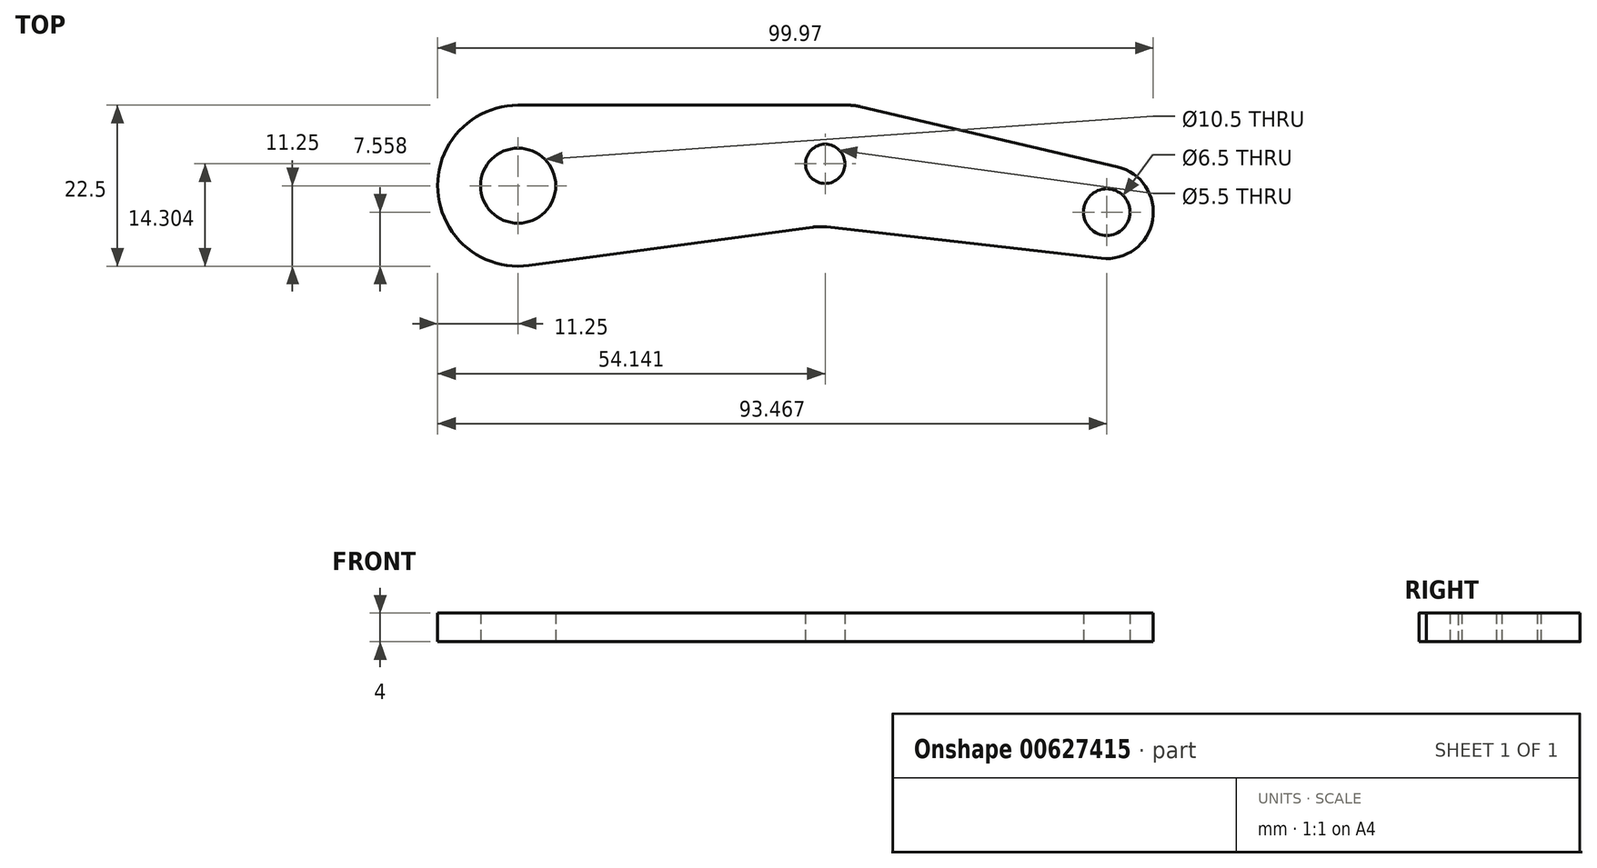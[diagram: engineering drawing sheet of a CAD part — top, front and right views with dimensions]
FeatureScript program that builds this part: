
annotation { "Feature Type Name" : "Feature", "Feature Type Description" : "" }
export const myFeature = defineFeature(function(context is Context, id is Id, definition is map)
    precondition{}
    {
        {
            var Q0;
            Q0=qCreatedBy(makeId("Top.planeOp"),FACE);
            var sketch = newSketch(context, id + "F0", { "sketchPlane" : qUnion([Q0])});
            skCircle(sketch, "E0", {"center": v(0, 0) * mm, "radius": 5.25 * mm});
            skArc(sketch, "E1", {"start": v(0, 11.25) * mm, "mid": v(-11.22, -0.76) * mm, "end": v(1.5, -11.15) * mm});
            skLineSegment(sketch, "E2", {"start": v(0, 11.25) * mm, "end": v(46.98, 11.25) * mm});
            skLineSegment(sketch, "E3", {"start": v(46.98, 11.25) * mm, "end": v(83.7, 2.64) * mm});
            skArc(sketch, "E4", {"start": v(81.48, -10.15) * mm, "mid": v(88.62, -4.8) * mm, "end": v(83.7, 2.64) * mm});
            skLineSegment(sketch, "E5", {"start": v(1.5, -11.15) * mm, "end": v(42.09, -5.66) * mm});
            skLineSegment(sketch, "E6", {"start": v(42.09, -5.66) * mm, "end": v(81.48, -10.15) * mm});
            skCircle(sketch, "E7", {"center": v(82.22, -3.7) * mm, "radius": 3.25 * mm});
            skCircle(sketch, "E8", {"center": v(42.9, 3.05) * mm, "radius": 2.75 * mm});
            skSolve(sketch);
        }
        {
            var Q0;
            Q0=makeQuery(id+"F0.imprint","IMPRINT",FACE,{"disambiguationData":[TD([[makeQuery(id+"F0.imprint","IMPRINT",EDGE,{"derivedFrom":sQuery(id+"F0.wireOp",EDGE,"E0")}),-1.0]])]});
            extrude(context, id + "F1", {"entities" : qUnion([Q0]), "depth" : 4 * mm, "offsetDistance" : 25 * mm});
        }
        {
            var Q0;
            Q0=makeQuery(id+"F1.opExtrude","SWEPT_EDGE",EDGE,{"disambiguationData":[OSD([sQuery(id+"F0.wireOp",EDGE,"E5"),sQuery(id+"F0.wireOp",EDGE,"E6")])]});
            var Q1;
            Q1=makeQuery(id+"F1.opExtrude","SWEPT_EDGE",EDGE,{"disambiguationData":[OSD([sQuery(id+"F0.wireOp",EDGE,"E2"),sQuery(id+"F0.wireOp",EDGE,"E3")])]});
            fillet(context, id + "F2", {"entities" : qUnion([Q0, Q1]), "radius" : 8 * mm, "tangentPropagation" : true, "allowEdgeOverflow" : false});
        }
    });
